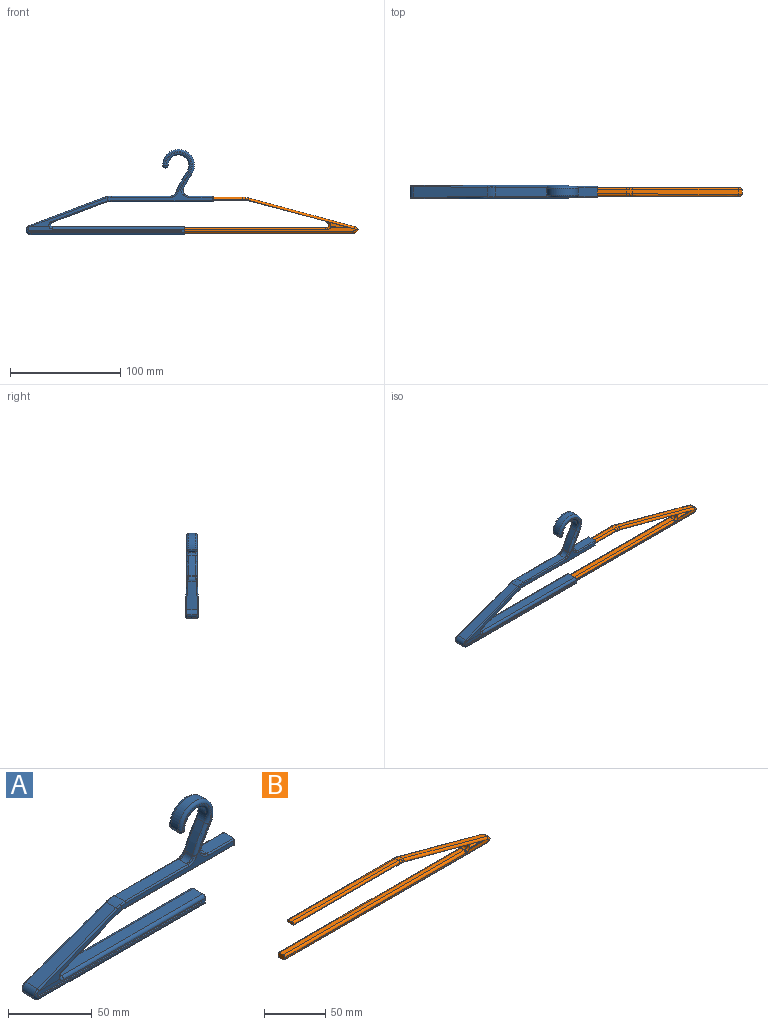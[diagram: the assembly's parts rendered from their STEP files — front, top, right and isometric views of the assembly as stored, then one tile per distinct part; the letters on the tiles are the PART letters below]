
ASSEMBLY  parts=2 mates=1
PART A: 104 faces, bbox 183.3x21.2x80.1 mm
  f0: plane 119.91x8mm, normal (0,0,1), area 959.3mm2, adj f5,f58,f93,f95
  f1: plane 141.15x4mm, normal (0,0,1), area 564.6mm2, adj f3,f5,f16,f18
  f2: plane 141.15x4mm, normal (0,0,-1), area 564.6mm2, adj f3,f5,f17,f19
  f3: plane 12x5mm, normal (1,0,0), area 40.6mm2, adj f1,f2,f6,f7,f10,f12,f13,f15
  f4: plane 139.36x8mm, normal (0,0,-1), area 1114.9mm2, adj f5,f57,f88,f90
  f5: plane 12x7mm, normal (1,0,0), area 44mm2, adj f0,f1,f2,f4,f6,f7,f8,f9
  f6: plane 142.4x5.04mm, normal (0,-1,0), area 326.5mm2, adj f3,f5,f13,f14,f15,f21,f64,f90
  f7: plane 142.4x5.04mm, normal (0,1,0), area 326.5mm2, adj f3,f5,f10,f11,f12,f23,f85,f88
  f8: plane 3x1mm, normal (0,1,0), area 3mm2, adj f5,f14,f18,f19
  f9: plane 3x1mm, normal (0,-1,0), area 3mm2, adj f5,f11,f16,f17
  f10: plane 138.15x2mm, normal (0,0,-1), area 276.3mm2, adj f3,f7,f11,f17
  f11: plane 2x1mm, normal (-1,0,0), area 2mm2, adj f7,f9,f10,f12
  f12: plane 138.15x2mm, normal (0,0,1), area 276.3mm2, adj f3,f7,f11,f16
  f13: plane 138.15x2mm, normal (0,0,1), area 276.3mm2, adj f3,f6,f14,f18
  f14: plane 2x1mm, normal (-1,0,0), area 2mm2, adj f6,f8,f13,f15
  f15: plane 138.15x2mm, normal (0,0,-1), area 276.3mm2, adj f3,f6,f14,f19
  f16: cylinder r=2mm len=141.15mm, axis (-1,0,0), area 443.4mm2, adj f1,f3,f5,f9,f12
  f17: cylinder r=2mm len=141.15mm, axis (1,0,0), area 443.4mm2, adj f2,f3,f5,f9,f10
  f18: cylinder r=2mm len=141.15mm, axis (1,0,0), area 443.4mm2, adj f1,f3,f5,f8,f13
  f19: cylinder r=2mm len=141.15mm, axis (-1,0,0), area 443.4mm2, adj f2,f3,f5,f8,f15
  f20: plane 67.23x25.41mm, normal (-0.35,0,0.94), area 649.1mm2, adj f48,f49,f67,f84
  f21: bspline ~73.88x27.92mm, area 215.1mm2, adj f6,f64,f67,f70,f75,f78,f79,f94
  f22: plane 46.96x17.78mm, normal (0.35,0,-0.94), area 443.9mm2, adj f56,f58,f79,f92,f94,f98
  f23: bspline ~74.62x28.2mm, area 215mm2, adj f7,f31,f83,f84,f85,f92,f97,f98
  f24: cylinder r=14.43mm len=28.86mm, axis (0,1,0), area 322.9mm2, adj f25,f29,f33,f39
  f25: cylinder r=2.5mm len=6mm, axis (0,1,0), area 47.1mm2, adj f24,f26,f34,f40
  f26: cylinder r=9.43mm len=18.86mm, axis (0,1,0), area 211mm2, adj f25,f27,f35,f41
  f27: cylinder r=111.94mm len=18.61mm, axis (0,1,0), area 126.9mm2, adj f26,f28,f36,f42
  f28: cylinder r=36.42mm len=6mm, axis (0,1,0), area 6mm2, adj f27,f37,f43,f54
  f29: cylinder r=106.94mm len=12.77mm, axis (0,1,0), area 88.3mm2, adj f24,f32,f38,f51
  f30: plane 96.36x45.91mm, normal (0,-1,0), area 383.8mm2, adj f38,f39,f40,f41,f42,f65,f66,f68
  f31: plane 96.15x44.7mm, normal (0,1,0), area 386.8mm2, adj f23,f32,f33,f34,f35,f36,f46,f80
  f32: torus R=108.94mm, axis (0,-1,0), area 51.8mm2, adj f29,f31,f33,f50
  f33: torus R=12.43mm, axis (0,-1,0), area 160.6mm2, adj f24,f31,f32,f34
  f34: torus R=0.5mm, axis (0,-1,0), area 17.5mm2, adj f25,f31,f33,f35
  f35: torus R=11.43mm, axis (0,-1,0), area 119mm2, adj f26,f31,f34,f36
  f36: torus R=109.94mm, axis (0,-1,0), area 65mm2, adj f27,f31,f35,f37,f53,f80
  f37: torus R=34.42mm, axis (0,-1,0), area 0.9mm2, adj f28,f36,f53
  f38: torus R=108.94mm, axis (0,-1,0), area 51.8mm2, adj f29,f30,f39,f52
  f39: torus R=12.43mm, axis (0,-1,0), area 160.6mm2, adj f24,f30,f38,f40
  f40: torus R=0.5mm, axis (0,-1,0), area 17.5mm2, adj f25,f30,f39,f41
  f41: torus R=11.43mm, axis (0,-1,0), area 119mm2, adj f26,f30,f40,f42
  f42: torus R=109.94mm, axis (0,-1,0), area 65mm2, adj f27,f30,f41,f43,f55,f65
  f43: torus R=34.42mm, axis (0,-1,0), area 0.9mm2, adj f28,f42,f55
  f44: plane 22.5x8mm, normal (0,0,1), area 179.4mm2, adj f46,f50,f51,f52,f69,f86
  f45: plane 92.49x8mm, normal (0,0,-1), area 739.9mm2, adj f46,f56,f74,f96
  f46: plane 9x5mm, normal (1,0,0), area 21.6mm2, adj f31,f44,f45,f59,f61,f62,f72,f86
  f47: plane 53.76x8.01mm, normal (0,0,1), area 429.5mm2, adj f49,f53,f54,f55,f68,f81
  f48: cylinder r=5mm len=10.2mm, axis (0,1,0), area 59.9mm2, adj f20,f57,f64,f85,f89,f91
  f49: cylinder r=20mm len=8.09mm, axis (0,-1,0), area 58mm2, adj f20,f47,f70,f71,f73,f82,f83
  f50: bspline ~8.27x7.7mm, area 18.1mm2, adj f32,f44,f51,f87
  f51: cylinder r=5mm len=7.17mm, axis (0,1,0), area 60.6mm2, adj f29,f44,f50,f52
  f52: bspline ~9.04x8.18mm, area 18.1mm2, adj f38,f44,f51,f66
  f53: bspline ~7.79x7.4mm, area 8.8mm2, adj f36,f37,f47,f54,f80
  f54: cylinder r=5mm len=6mm, axis (0,1,0), area 36mm2, adj f28,f47,f53,f55
  f55: bspline ~7.4x7.19mm, area 8.8mm2, adj f42,f43,f47,f54,f65
  f56: cylinder r=20mm len=8.12mm, axis (0,-1,0), area 58.1mm2, adj f22,f45,f76,f77,f78,f97,f99
  f57: cylinder r=5mm len=8mm, axis (0,-1,0), area 51mm2, adj f4,f48,f89,f91
  f58: cylinder r=2mm len=8mm, axis (0,-1,0), area 44.5mm2, adj f0,f22,f92,f94
  f59: plane 95x5.8mm, normal (0,0,-1), area 551mm2, adj f46,f63,f100,f103
  f60: plane 95x0.8mm, normal (0,1,0), area 76mm2, adj f63,f72,f100,f101
  f61: plane 95x5.8mm, normal (0,0,1), area 551mm2, adj f46,f63,f101,f102
  f62: plane 95x0.8mm, normal (0,-1,0), area 76mm2, adj f46,f63,f102,f103
  f63: plane 8x3mm, normal (1,0,0), area 23mm2, adj f59,f60,f61,f62,f100,f101,f102,f103
  f64: bspline ~4.41x4.35mm, area 4.5mm2, adj f6,f21,f48,f67,f91
  f65: bspline ~8.9x5.99mm, area 9.9mm2, adj f30,f42,f55,f68
  f66: bspline ~8.99x6mm, area 6mm2, adj f30,f52,f69
  f67: bspline ~98.16x37.86mm, area 111.8mm2, adj f20,f21,f64,f70
  f68: cylinder r=1mm len=53.75mm, axis (1,0,0), area 84.4mm2, adj f30,f47,f65,f71
  f69: cylinder r=1mm len=22.5mm, axis (1,0,0), area 34.6mm2, adj f30,f44,f66,f72
  f70: bspline ~6.03x2.83mm, area 5.2mm2, adj f21,f49,f67,f73
  f71: torus R=19mm, axis (0,-1,0), area 6mm2, adj f30,f49,f68,f73
  f72: cylinder r=1mm len=5mm, axis (0,0,-1), area 6.3mm2, adj f30,f46,f60,f69,f74
  f73: bspline ~1.04x1.01mm, area 0mm2, adj f49,f70,f71,f75
  f74: cylinder r=1mm len=92.49mm, axis (-1,0,0), area 144.5mm2, adj f30,f45,f72,f76
  f75: bspline ~4.51x0.02mm, area 0mm2, adj f21,f30,f73,f77
  f76: torus R=21mm, axis (0,-1,0), area 5.6mm2, adj f30,f56,f74,f77
  f77: bspline ~1.04x1.03mm, area 0mm2, adj f56,f75,f76,f78
  f78: bspline ~7.98x3.14mm, area 5.9mm2, adj f21,f56,f77,f79
  f79: bspline ~66.4x25.91mm, area 78.3mm2, adj f21,f22,f78,f94
  f80: bspline ~8.9x5.99mm, area 9.9mm2, adj f31,f36,f53,f81
  f81: cylinder r=1mm len=53.75mm, axis (-1,0,0), area 84.4mm2, adj f31,f47,f80,f82
  f82: torus R=19mm, axis (0,-1,0), area 6mm2, adj f31,f49,f81,f83
  f83: bspline ~6.03x2.83mm, area 5.2mm2, adj f23,f31,f49,f82,f84
  f84: bspline ~98.18x37.86mm, area 111.8mm2, adj f20,f23,f83,f85
  f85: bspline ~4.41x4.35mm, area 4.5mm2, adj f7,f23,f48,f84,f89
  f86: cylinder r=1mm len=22.5mm, axis (-1,0,0), area 35.3mm2, adj f31,f44,f46,f87
  f87: bspline ~8.99x6mm, area 6.2mm2, adj f31,f50,f86
  f88: cylinder r=2mm len=139.36mm, axis (1,0,0), area 437.8mm2, adj f4,f5,f7,f89
  f89: torus R=3mm, axis (0,-1,0), area 22mm2, adj f7,f48,f57,f85,f88
  f90: cylinder r=2mm len=139.36mm, axis (-1,0,0), area 437.8mm2, adj f4,f5,f6,f91
  f91: torus R=3mm, axis (0,-1,0), area 22mm2, adj f6,f48,f57,f64,f90
  f92: torus R=4mm, axis (0,-1,0), area 21.6mm2, adj f7,f22,f23,f58,f93,f98
  f93: cylinder r=2mm len=119.91mm, axis (-1,0,0), area 376.7mm2, adj f0,f5,f7,f92
  f94: torus R=4mm, axis (0,-1,0), area 21.6mm2, adj f6,f21,f22,f58,f79,f95
  f95: cylinder r=2mm len=119.91mm, axis (1,0,0), area 376.7mm2, adj f0,f5,f6,f94
  f96: cylinder r=1mm len=92.49mm, axis (1,0,0), area 145.3mm2, adj f31,f45,f46,f97
  f97: torus R=21mm, axis (0,-1,0), area 5.6mm2, adj f23,f31,f56,f96,f99
  f98: bspline ~76.8x29.85mm, area 78.3mm2, adj f22,f23,f92,f99
  f99: bspline ~7.98x3.14mm, area 5.9mm2, adj f23,f56,f97,f98
  f100: cylinder r=1.1mm len=95mm, axis (-1,0,0), area 164.1mm2, adj f46,f59,f60,f63
  f101: cylinder r=1.1mm len=95mm, axis (-1,0,0), area 164.1mm2, adj f46,f60,f61,f63
  f102: cylinder r=1.1mm len=95mm, axis (-1,0,0), area 164.1mm2, adj f46,f61,f62,f63
  f103: cylinder r=1.1mm len=95mm, axis (-1,0,0), area 164.1mm2, adj f46,f59,f62,f63
PART B: 41 faces, bbox 272.3x8.3x43.5 mm
  f0: plane 122.34x3.6mm, normal (0,0,1), area 440.4mm2, adj f4,f15,f27,f34
  f1: plane 125x0.77mm, normal (0,-1,0), area 75mm2, adj f2,f4,f6,f14,f32,f33,f34
  f2: plane 122.41x7.6mm, normal (0,0,-1), area 930.3mm2, adj f1,f3,f4,f14
  f3: plane 125x0.77mm, normal (0,1,0), area 75mm2, adj f2,f4,f8,f14,f25,f26,f27
  f4: plane 7.6x2.6mm, normal (-1,0,0), area 18mm2, adj f0,f1,f2,f3,f27,f34
  f5: plane 96.12x26.03mm, normal (0.26,0,0.97), area 379.4mm2, adj f15,f17,f24,f31
  f6: bspline ~102.38x27.72mm, area 63.3mm2, adj f1,f7,f12,f14,f18,f31,f32,f38
  f7: plane 69.29x18.25mm, normal (-0.25,0,-0.97), area 555.7mm2, adj f6,f8,f14,f18
  f8: bspline ~102.38x27.72mm, area 63.3mm2, adj f3,f7,f13,f14,f18,f24,f25,f35
  f9: plane 208.1x4mm, normal (0,0,1), area 832.4mm2, adj f10,f19,f37,f40
  f10: plane 8x5mm, normal (-1,0,0), area 36.6mm2, adj f9,f11,f12,f13,f21,f28,f37,f40
  f11: plane 232.62x4mm, normal (0,0,-1), area 930.5mm2, adj f10,f16,f21,f28
  f12: plane 235.15x3.07mm, normal (0,-1,0), area 279.1mm2, adj f6,f10,f28,f29,f30,f31,f38,f39
  f13: plane 235.15x3.07mm, normal (0,1,0), area 279.1mm2, adj f8,f10,f21,f22,f23,f24,f35,f36
  f14: cylinder r=20mm len=7.61mm, axis (0,-1,0), area 39.2mm2, adj f1,f2,f3,f6,f7,f8
  f15: cylinder r=20mm len=5.23mm, axis (0,-1,0), area 19mm2, adj f0,f5,f25,f26,f32,f33
  f16: cylinder r=5mm len=4.62mm, axis (0,1,0), area 23.6mm2, adj f11,f17,f22,f29
  f17: cylinder r=5mm len=4.05mm, axis (0,-1,0), area 18.4mm2, adj f5,f16,f22,f23,f29,f30
  f18: cylinder r=5mm len=7.91mm, axis (0,1,0), area 35.2mm2, adj f6,f7,f8,f20,f35,f38
  f19: cylinder r=5mm len=4mm, axis (0,-1,0), area 3.9mm2, adj f9,f20,f36,f39
  f20: cylinder r=2mm len=4mm, axis (0,-1,0), area 12.8mm2, adj f18,f19,f35,f38
  f21: cylinder r=2mm len=232.62mm, axis (1,0,0), area 730.8mm2, adj f10,f11,f13,f22
  f22: torus R=3mm, axis (0,-1,0), area 15mm2, adj f13,f16,f17,f21,f23
  f23: bspline ~4.48x4.36mm, area 9.7mm2, adj f13,f17,f22,f24
  f24: bspline ~154.07x43.48mm, area 311.9mm2, adj f5,f8,f13,f23,f25
  f25: bspline ~6.15x3.22mm, area 7mm2, adj f3,f8,f15,f24,f26
  f26: torus R=18mm, axis (0,1,0), area 9mm2, adj f3,f15,f25,f27
  f27: cylinder r=2mm len=122.34mm, axis (1,0,0), area 384.3mm2, adj f0,f3,f4,f26
  f28: cylinder r=2mm len=232.62mm, axis (-1,0,0), area 730.8mm2, adj f10,f11,f12,f29
  f29: torus R=3mm, axis (0,-1,0), area 15mm2, adj f12,f16,f17,f28,f30
  f30: bspline ~4.48x4.37mm, area 9.7mm2, adj f12,f17,f29,f31
  f31: bspline ~154.07x43.48mm, area 311.9mm2, adj f5,f6,f12,f30,f32
  f32: bspline ~6.15x3.22mm, area 7mm2, adj f1,f6,f15,f31,f33
  f33: torus R=18mm, axis (0,-1,0), area 9mm2, adj f1,f15,f32,f34
  f34: cylinder r=2mm len=122.34mm, axis (1,0,0), area 384.3mm2, adj f0,f1,f4,f33
  f35: torus R=4mm, axis (0,-1,0), area 19.7mm2, adj f8,f13,f18,f20,f36
  f36: torus R=7mm, axis (0,-1,0), area 3.5mm2, adj f13,f19,f35,f37
  f37: cylinder r=2mm len=208.1mm, axis (-1,0,0), area 653.8mm2, adj f9,f10,f13,f36
  f38: torus R=4mm, axis (0,-1,0), area 19.7mm2, adj f6,f12,f18,f20,f39
  f39: torus R=7mm, axis (0,-1,0), area 3.5mm2, adj f12,f19,f38,f40
  f40: cylinder r=2mm len=208.1mm, axis (1,0,0), area 653.8mm2, adj f9,f10,f12,f39
PLACE A t=(-57.26,-28.66,30.76)mm
PLACE B t=(-128.06,-28.66,30.96)mm
MATE slider B.f4 <-> A.f46  axis (-1,0,0) through (-121.42,-28.66,48.2)mm
